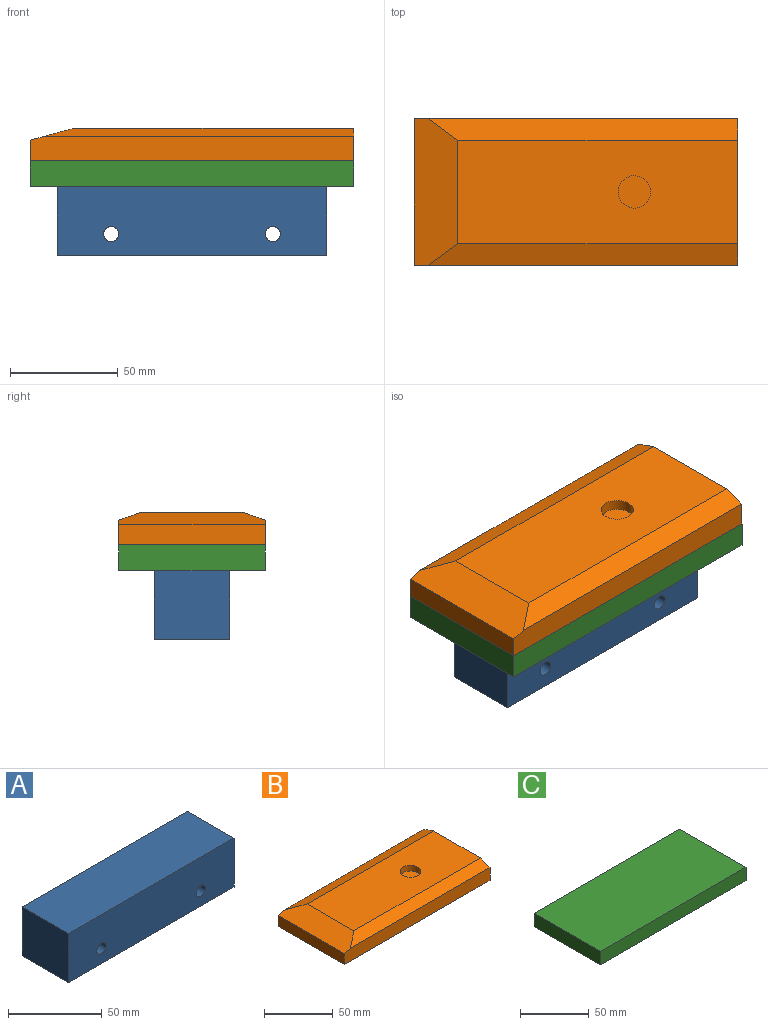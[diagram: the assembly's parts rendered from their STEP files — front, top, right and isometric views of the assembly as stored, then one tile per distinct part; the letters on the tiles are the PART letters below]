
ASSEMBLY  parts=3 mates=2
PART A: 8 faces, bbox 125x35x32 mm
  f0: plane 125x35mm, normal (0,0,1), area 4375mm2, adj f1,f3,f6,f7
  f1: plane 35x32mm, normal (-1,0,0), area 1120mm2, adj f0,f2,f6,f7
  f2: plane 125x35mm, normal (0,0,-1), area 4375mm2, adj f1,f3,f6,f7
  f3: plane 35x32mm, normal (1,0,0), area 1120mm2, adj f0,f2,f6,f7
  f4: cylinder r=3.5mm len=35mm, axis (0,1,0), area 769.7mm2, adj f6,f7
  f5: cylinder r=3.5mm len=35mm, axis (0,1,0), area 769.7mm2, adj f6,f7
  f6: plane 125x32mm, normal (0,-1,0), area 3923mm2, adj f0,f1,f2,f3,f4,f5
  f7: plane 125x32mm, normal (0,1,0), area 3923mm2, adj f0,f1,f2,f3,f4,f5
PART B: 11 faces, bbox 150x68x15 mm
  f0: plane 150x11.36mm, normal (0,1,0), area 1698.5mm2, adj f1,f3,f5,f8,f9
  f1: plane 68x9.64mm, normal (-1,0,0), area 655.6mm2, adj f0,f2,f5,f8
  f2: plane 150x11.36mm, normal (0,-1,0), area 1698.5mm2, adj f1,f3,f5,f8,f10
  f3: plane 68x15mm, normal (1,0,0), area 983.6mm2, adj f0,f2,f4,f5,f9,f10
  f4: plane 130x48mm, normal (0,0,1), area 6063.3mm2, adj f3,f6,f8,f9,f10
  f5: plane 150x68mm, normal (0,0,-1), area 10200mm2, adj f0,f1,f2,f3
  f6: cylinder r=7.5mm len=15mm, axis (0,0,1), area 235.6mm2, adj f4,f7
  f7: plane 15x15mm, normal (0,0,1), area 176.7mm2, adj f6
  f8: plane 68x20mm, normal (-0.26,0,0.97), area 1267.3mm2, adj f0,f1,f2,f4,f9,f10
  f9: plane 143.58x10mm, normal (0,0.34,0.94), area 1455.7mm2, adj f0,f3,f4,f8
  f10: plane 143.58x10mm, normal (0,-0.34,0.94), area 1455.7mm2, adj f2,f3,f4,f8
PART C: 6 faces, bbox 150x68x12 mm
  f0: plane 150x12mm, normal (0,1,0), area 1800mm2, adj f1,f3,f4,f5
  f1: plane 68x12mm, normal (-1,0,0), area 816mm2, adj f0,f2,f4,f5
  f2: plane 150x12mm, normal (0,-1,0), area 1800mm2, adj f1,f3,f4,f5
  f3: plane 68x12mm, normal (1,0,0), area 816mm2, adj f0,f2,f4,f5
  f4: plane 150x68mm, normal (0,0,1), area 10200mm2, adj f0,f1,f2,f3
  f5: plane 150x68mm, normal (0,0,-1), area 10200mm2, adj f0,f1,f2,f3
PLACE A t=(-26.98,-2.01,2.39)mm fixed
PLACE B t=(21.22,-14.68,27.38)mm
PLACE C t=(5.21,-23.21,15.38)mm
MATE fastened C.f5 <-> A.f0  axis (0,0,-1) through (9.18,-2.01,15.38)mm
MATE fastened B.f5 <-> C.f4  axis (0,0,-1) through (84.18,-2.01,27.38)mm
